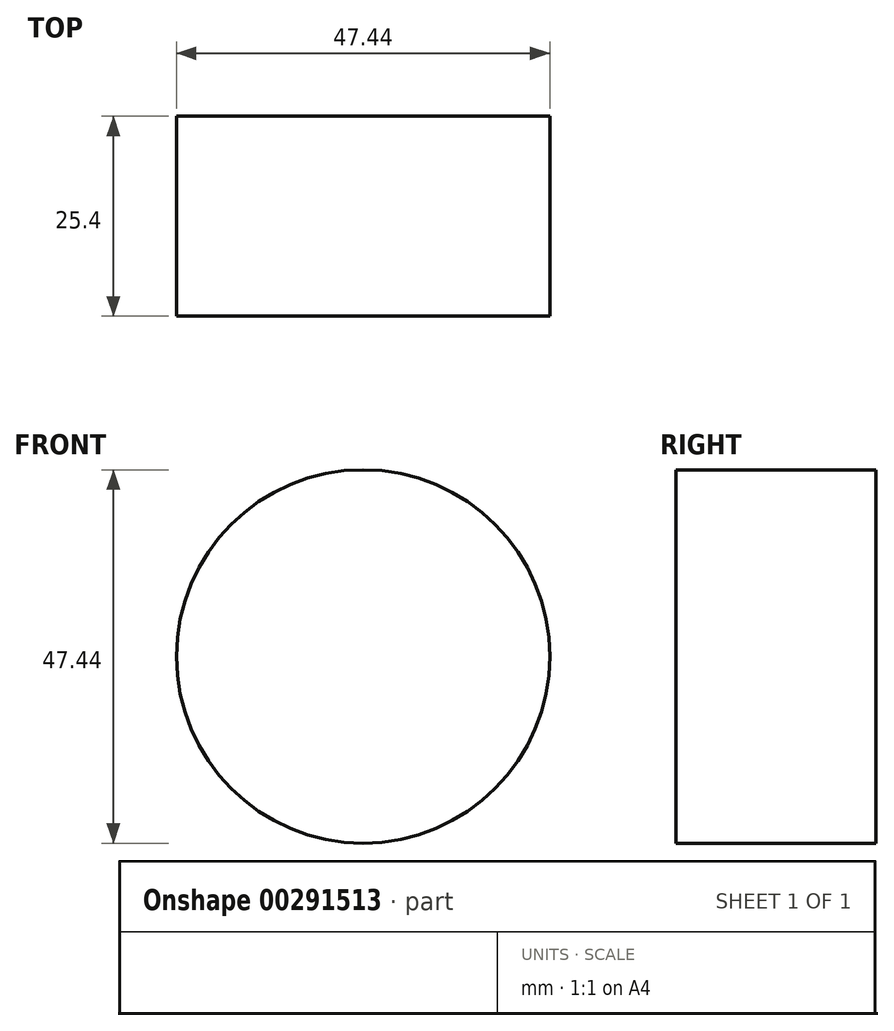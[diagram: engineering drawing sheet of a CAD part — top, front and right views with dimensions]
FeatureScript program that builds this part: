
annotation { "Feature Type Name" : "Feature", "Feature Type Description" : "" }
export const myFeature = defineFeature(function(context is Context, id is Id, definition is map)
    precondition{}
    {
        {
            var Q0;
            Q0=qCreatedBy(makeId("Front.planeOp"),FACE);
            var sketch = newSketch(context, id + "F0", { "sketchPlane" : qUnion([Q0])});
            skCircle(sketch, "E0", {"center": v(0, 0) * mm, "radius": 23.72 * mm});
            skSolve(sketch);
        }
        {
            var Q0;
            Q0=makeQuery(id+"F0.imprint","IMPRINT",FACE,{"disambiguationData":[TD([[makeQuery(id+"F0.imprint","IMPRINT",EDGE,{"derivedFrom":sQuery(id+"F0.wireOp",EDGE,"E0")}),1.0]])]});
            extrude(context, id + "F1", {"entities" : qUnion([Q0]), "endBound" : BoundingType.SYMMETRIC, "depth" : 25.4 * mm});
        }
    });
